# Revit family: KATON
name_source: partatom
category: Luminaires
units: mm (PartAtom-declared; Revit-internal decimal feet)

## family parameters
Cote de connecteur circulaire = Utiliser le diamètre
Couper avec des vides une fois chargée = Oui
Hôte = Face
Numéro OmniClass = 23.80.70.11.17
Partagée = Oui
Point de calcul de pièce = Oui
Source d'éclairage = Oui
Titre OmniClass = Specialized Lighting by Location or Use
Type d'élément = Normal

## types (4) — shared parameters
Angle de l'inclinaison = 60.00°
Distance bord corps = 24 mm  [stored 0.0787402 ft]
Emettre la visibilité des formes dans le rendu = Non
Emettre à partir de la largeur du rectangle = 610 mm
Emettre à partir de la longueur du rectangle = 1219 mm
Fabricant = Résistex
Filtre de couleur = 16777215
Garantie = 5 ans
Gradation des changements de température de couleur de lampe = <Aucun>
IK = 04
IP = 40
Image du type = <Aucun>
Indice de charge = Eclairage
Largeur = 595 mm  [stored 1.9521 ft]
Largeur 2 = 554 mm  [stored 1.81759 ft]
Longueur = 595 mm  [stored 1.9521 ft]
Longueur 2 = 554 mm  [stored 1.81759 ft]
Matériau corps = Alu blanc
Matériau diffuseur = PC Transparent
Modèle = Katon
Nombre pôles = 1
Tension = 230 V
URL = https://www.resistex-sa.com
Épaisseur = 26 mm
Épaisseur 2 = 2 mm  [stored 0.00656168 ft]
zero-valued in all types: Elévation par défaut

## per-type parameters (varying)
| type | Charge apparente | Commentaires relatifs à la puissance | Coût | Description | Fichier de distribution photométrique |
| 621302 | 41 VA | 38.9W | 40 $ | Encastré tertiaire équipé d'une platine LED SMD, efficacité lumineuse de 104.7lm/W | 621302.ies |
| 621303 | 42 VA | 40.3W | 40 $ | Encastré tertiaire équipé d'une platine LED SMD, efficacité lumineuse de 105.4lm/W | 621303.ies |
| 621304 | 40 VA | 38.9W | 67.5 $ | Encastré tertiaire équipé d'une platine LED SMD, efficacité lumineuse de 104.7lm/W | 621304.ies |
| 621305 | 42 VA | 40.3W | 67.5 $ | Encastré tertiaire équipé d'une platine LED SMD, efficacité lumineuse de 105.4lm/W | 621305.ies |

note: [stored X ft] marks values corroborated as IEEE doubles in the binary element streams (Revit-internal decimal feet)
